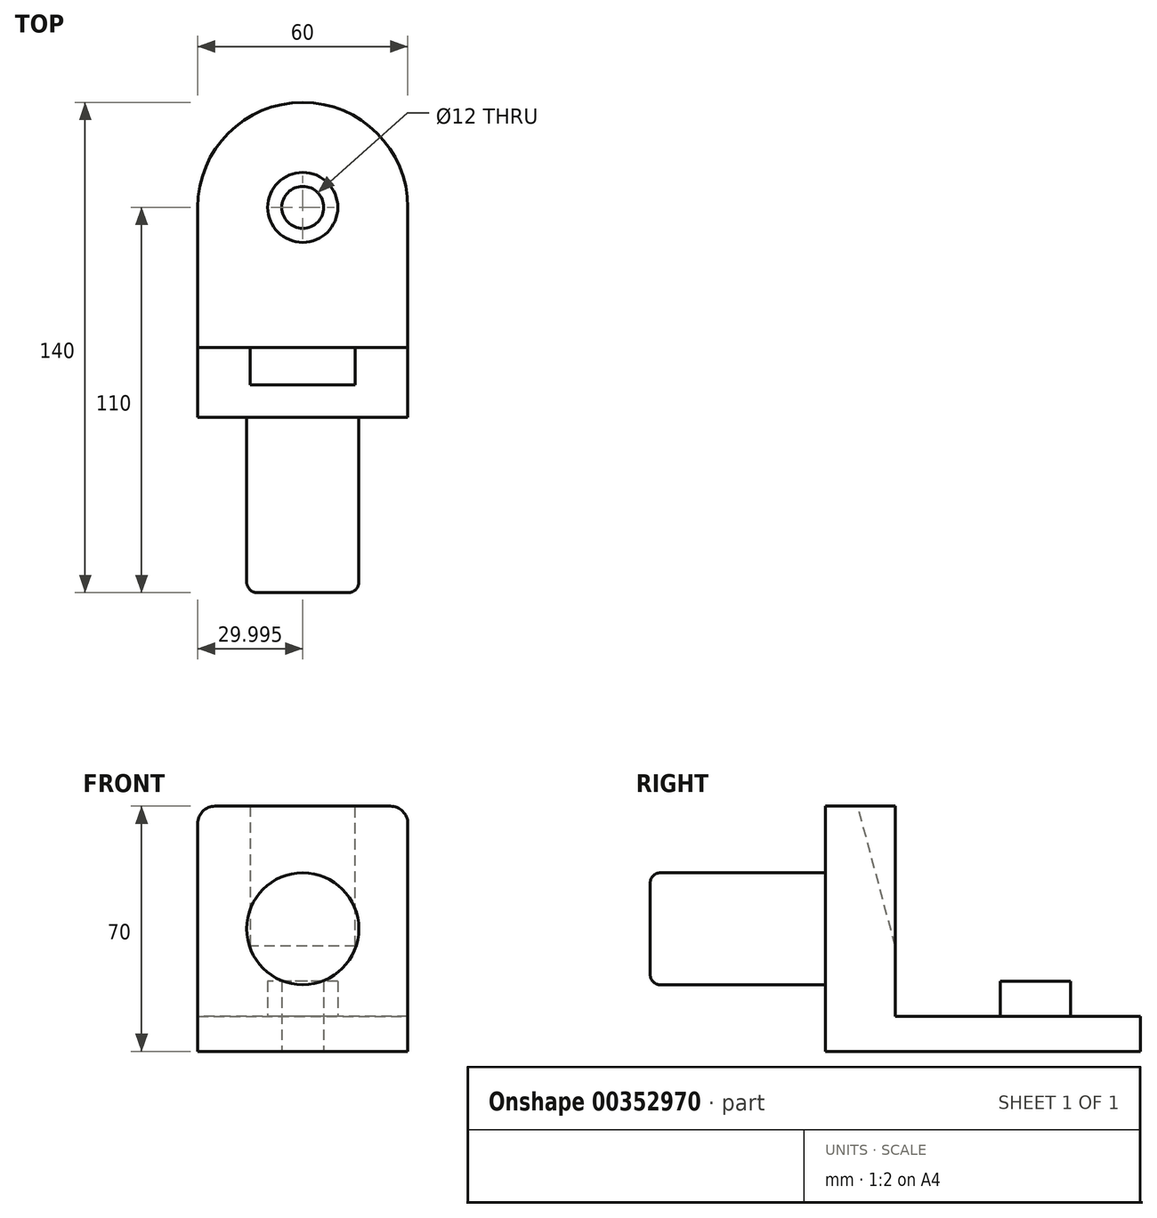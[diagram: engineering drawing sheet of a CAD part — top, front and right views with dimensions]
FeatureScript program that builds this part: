
annotation { "Feature Type Name" : "Feature", "Feature Type Description" : "" }
export const myFeature = defineFeature(function(context is Context, id is Id, definition is map)
    precondition{}
    {
        {
            var Q0;
            Q0=qCreatedBy(makeId("Top.planeOp"),FACE);
            var sketch = newSketch(context, id + "F0", { "sketchPlane" : qUnion([Q0])});
            skLineSegment(sketch, "E0", {"start": v(-38.74, 0) * mm, "end": v(-38.74, 40) * mm});
            skLineSegment(sketch, "E1", {"start": v(-8.74, 70) * mm, "end": v(-8.74, 70) * mm});
            skLineSegment(sketch, "E2", {"start": v(21.26, 40) * mm, "end": v(21.26, 0) * mm});
            skLineSegment(sketch, "E3", {"start": v(21.26, 0) * mm, "end": v(21.26, -20) * mm});
            skLineSegment(sketch, "E4", {"start": v(-38.74, 0) * mm, "end": v(-38.74, -20) * mm});
            skLineSegment(sketch, "E5", {"start": v(-38.74, -20) * mm, "end": v(21.26, -20) * mm});
            skPoint(sketch, "E6.visualSharp", {"position": v(-38.74, 70) * mm});
            skArc(sketch, "E6.filletArc", {"start": v(-8.74, 70) * mm, "mid": v(-29.96, 61.21) * mm, "end": v(-38.74, 40) * mm});
            skPoint(sketch, "E7.visualSharp", {"position": v(21.26, 70) * mm});
            skArc(sketch, "E7.filletArc", {"start": v(21.26, 40) * mm, "mid": v(12.47, 61.21) * mm, "end": v(-8.74, 70) * mm});
            skCircle(sketch, "E8", {"center": v(-8.74, 40) * mm, "radius": 10 * mm});
            skCircle(sketch, "E9", {"center": v(-8.74, 40) * mm, "radius": 6 * mm});
            skLineSegment(sketch, "E10", {"start": v(-38.74, 0) * mm, "end": v(21.26, 0) * mm});
            skSolve(sketch);
        }
        {
            var Q0;
            Q0=makeQuery(id+"F0.imprint","IMPRINT",FACE,{"disambiguationData":[TD([[makeQuery(id+"F0.imprint","IMPRINT",EDGE,{"derivedFrom":sQuery(id+"F0.wireOp",EDGE,"E0")}),-1.0]])]});
            extrude(context, id + "F1", {"entities" : qUnion([Q0]), "depth" : 10 * mm});
        }
        {
            var Q0;
            Q0=makeQuery(id+"F0.imprint","IMPRINT",FACE,{"disambiguationData":[TD([[makeQuery(id+"F0.imprint","IMPRINT",EDGE,{"derivedFrom":sQuery(id+"F0.wireOp",EDGE,"E8")}),1.0]])]});
            extrude(context, id + "F2", {"entities" : qUnion([Q0]), "operationType" : NewBodyOperationType.ADD, "depth" : 20 * mm});
        }
        {
            var Q0;
            Q0=makeQuery(id+"F0.imprint","IMPRINT",FACE,{"disambiguationData":[TD([[makeQuery(id+"F0.imprint","IMPRINT",EDGE,{"derivedFrom":sQuery(id+"F0.wireOp",EDGE,"E3")}),-1.0]])]});
            extrude(context, id + "F3", {"entities" : qUnion([Q0]), "operationType" : NewBodyOperationType.ADD, "depth" : 70 * mm});
        }
        {
            var Q0;
            Q0=makeQuery(id+"F3.opExtrude","SWEPT_FACE",FACE,{"disambiguationData":[OSD([sQuery(id+"F0.wireOp",EDGE,"E5")])]});
            var sketch = newSketch(context, id + "F4", { "sketchPlane" : qUnion([Q0])});
            skCircle(sketch, "E11", {"center": v(-8.74, 35) * mm, "radius": 16 * mm});
            skPoint(sketch, "E12.orphan", {"position": v(-38.74, 35) * mm});
            skPoint(sketch, "E13.orphan", {"position": v(-8.74, 70) * mm});
            skPoint(sketch, "E14.end.orphan", {"position": v(21.26, 35) * mm});
            skPoint(sketch, "E15.orphan", {"position": v(-8.74, 0) * mm});
            skSolve(sketch);
        }
        {
            var Q0;
            Q0=makeQuery(id+"F4.imprint","IMPRINT",FACE,{"disambiguationData":[TD([[makeQuery(id+"F4.imprint","IMPRINT",EDGE,{"derivedFrom":sQuery(id+"F4.wireOp",EDGE,"E11")}),1.0]])]});
            extrude(context, id + "F5", {"entities" : qUnion([Q0]), "operationType" : NewBodyOperationType.ADD, "depth" : 50 * mm});
        }
        {
            var Q0;
            Q0=makeQuery(id+"F5.opExtrude","CAP_EDGE",EDGE,{"disambiguationData":[OSD([sQuery(id+"F4.wireOp",EDGE,"E11")])],"isStart":false});
            fillet(context, id + "F6", {"entities" : qUnion([Q0]), "radius" : 3 * mm, "tangentPropagation" : true, "allowEdgeOverflow" : false});
        }
        {
            var Q0;
            Q0=makeQuery(id+"F3.boolean.opBoolean","MERGE",FACE,{"derivedFrom":[makeQuery(id+"F1.opExtrude","SWEPT_FACE",FACE,{"disambiguationData":[OSD([sQuery(id+"F0.wireOp",EDGE,"E2")])]}),makeQuery(id+"F3.opExtrude","SWEPT_FACE",FACE,{"disambiguationData":[OSD([sQuery(id+"F0.wireOp",EDGE,"E3")])]})]});
            var sketch = newSketch(context, id + "F7", { "sketchPlane" : qUnion([Q0])});
            skLineSegment(sketch, "E16", {"start": v(0, 70) * mm, "end": v(0, 30) * mm});
            skLineSegment(sketch, "E17", {"start": v(0, 30) * mm, "end": v(-10.72, 70) * mm});
            skLineSegment(sketch, "E18", {"start": v(-10.72, 70) * mm, "end": v(0, 70) * mm});
            skSolve(sketch);
        }
        {
            var Q0;
            Q0=makeQuery(id+"F3.boolean.opBoolean","MERGE",FACE,{"derivedFrom":[makeQuery(id+"F1.opExtrude","SWEPT_FACE",FACE,{"disambiguationData":[OSD([sQuery(id+"F0.wireOp",EDGE,"E0")])]}),makeQuery(id+"F3.opExtrude","SWEPT_FACE",FACE,{"disambiguationData":[OSD([sQuery(id+"F0.wireOp",EDGE,"E4")])]})]});
            var sketch = newSketch(context, id + "F8", { "sketchPlane" : qUnion([Q0])});
            skLineSegment(sketch, "E19", {"start": v(0, 70) * mm, "end": v(0, 30) * mm});
            skLineSegment(sketch, "E20", {"start": v(0, 30) * mm, "end": v(10.72, 70) * mm});
            skLineSegment(sketch, "E21", {"start": v(10.72, 70) * mm, "end": v(0, 70) * mm});
            skSolve(sketch);
        }
        {
            var Q0;
            Q0=makeQuery(id+"F8.imprint","IMPRINT",FACE,{"disambiguationData":[TD([[makeQuery(id+"F8.imprint","IMPRINT",EDGE,{"derivedFrom":sQuery(id+"F8.wireOp",EDGE,"E19")}),1.0]])]});
            extrude(context, id + "F9", {"entities" : qUnion([Q0]), "operationType" : NewBodyOperationType.REMOVE, "oppositeDirection" : true, "depth" : 65.4 * mm});
        }
        {
            var Q0;
            {var subQ4=sQuery(id+"F8.wireOp",EDGE,"E20");Q0=makeQuery(id+"F8.imprint","IMPRINT",FACE,{"disambiguationData":[TD([[makeQuery(id+"F8.imprint","IMPRINT",EDGE,{"derivedFrom":subQ4}),-1.0]])]});}
            var Q1;
            Q1=makeQuery(id+"F8.imprint","IMPRINT",FACE,{"disambiguationData":[TD([[makeQuery(id+"F8.imprint","IMPRINT",EDGE,{"derivedFrom":sQuery(id+"F8.wireOp",EDGE,"E19")}),1.0]])]});
            extrude(context, id + "F10", {"entities" : qUnion([Q0, Q1]), "operationType" : NewBodyOperationType.ADD, "oppositeDirection" : true, "depth" : 15 * mm});
        }
        {
            var Q0;
            {var subQ4=sQuery(id+"F7.wireOp",EDGE,"E17");Q0=makeQuery(id+"F7.imprint","IMPRINT",FACE,{"disambiguationData":[TD([[makeQuery(id+"F7.imprint","IMPRINT",EDGE,{"derivedFrom":subQ4}),1.0]])]});}
            var Q1;
            Q1=makeQuery(id+"F7.imprint","IMPRINT",FACE,{"disambiguationData":[TD([[makeQuery(id+"F7.imprint","IMPRINT",EDGE,{"derivedFrom":sQuery(id+"F7.wireOp",EDGE,"E16")}),-1.0]])]});
            extrude(context, id + "F11", {"entities" : qUnion([Q0, Q1]), "operationType" : NewBodyOperationType.ADD, "oppositeDirection" : true, "depth" : 15 * mm});
        }
        {
            var Q0;
            {var subQ0=sQuery(id+"F0.wireOp",EDGE,"E3");Q0=makeQuery(id+"F11.boolean.opBoolean","MERGE",EDGE,{"derivedFrom":[makeQuery(id+"F3.opExtrude","CAP_EDGE",EDGE,{"disambiguationData":[OSD([subQ0])],"isStart":false}),makeQuery(id+"F11.opExtrude","CAP_EDGE",EDGE,{"disambiguationData":[OSD([subQ0,sQuery(id+"F7.wireOp",EDGE,"E18")])],"isStart":true})]});}
            fillet(context, id + "F12", {"entities" : qUnion([Q0]), "radius" : 5 * mm, "tangentPropagation" : true, "allowEdgeOverflow" : false});
        }
        {
            var Q0;
            {var subQ0=sQuery(id+"F0.wireOp",EDGE,"E4");Q0=makeQuery(id+"F10.boolean.opBoolean","MERGE",EDGE,{"derivedFrom":[makeQuery(id+"F3.opExtrude","CAP_EDGE",EDGE,{"disambiguationData":[OSD([subQ0])],"isStart":false}),makeQuery(id+"F10.opExtrude","CAP_EDGE",EDGE,{"disambiguationData":[OSD([subQ0,sQuery(id+"F8.wireOp",EDGE,"E21")])],"isStart":true})]});}
            fillet(context, id + "F13", {"entities" : qUnion([Q0]), "radius" : 5 * mm, "tangentPropagation" : true, "allowEdgeOverflow" : false});
        }
    });
